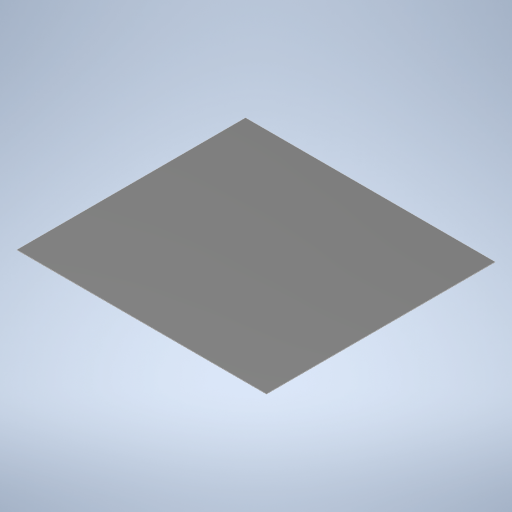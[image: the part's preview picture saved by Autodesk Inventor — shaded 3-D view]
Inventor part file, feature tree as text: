
AUTODESK INVENTOR PART (.ipt)
format: ipt  version: 2023 (Build 270158000, 158)  size: 205,824 bytes
history: native  units: in
note: dims shown in document units (in); Inventor stores cm internally (conversion verified against a paired STEP export)
features: extrude x1, sketch x1
ambient origin geometry x8: Origin, YZ Plane, XZ Plane, XY Plane, X Axis, Y Axis, Z Axis, Center Point
bodies: Solid1 (feature_tree)
feature tree (2):
  extrude  "Extrusion1"  Depth=1.874in
  sketch  "Sketch1"  dims[d0=1.7165in d1=1.874in d2=0.0031in d3=0.0in]
